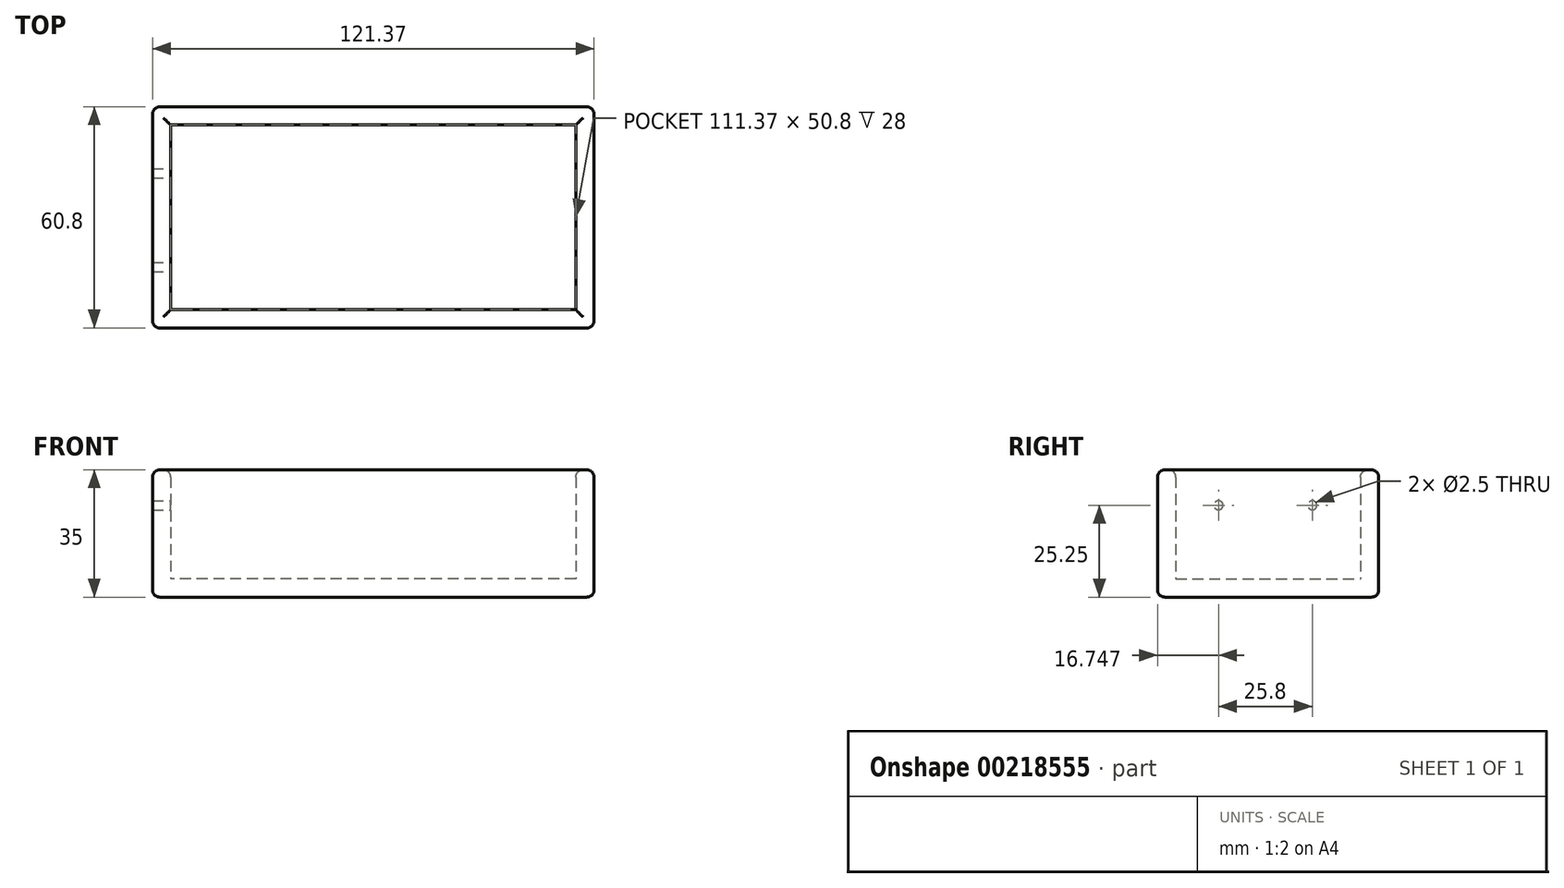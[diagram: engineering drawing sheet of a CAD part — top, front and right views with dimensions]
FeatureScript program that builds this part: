
annotation { "Feature Type Name" : "Feature", "Feature Type Description" : "" }
export const myFeature = defineFeature(function(context is Context, id is Id, definition is map)
    precondition{}
    {
        {
            var Q0;
            Q0=qCreatedBy(makeId("Top.planeOp"),FACE);
            var sketch = newSketch(context, id + "F0", { "sketchPlane" : qUnion([Q0])});
            skLineSegment(sketch, "E0.bottom", {"start": v(-56.15, 22.89) * mm, "end": v(55.22, 22.89) * mm});
            skLineSegment(sketch, "E0.top", {"start": v(-56.15, -27.91) * mm, "end": v(55.22, -27.91) * mm});
            skLineSegment(sketch, "E0.left", {"start": v(-56.15, 22.89) * mm, "end": v(-56.15, -27.91) * mm});
            skLineSegment(sketch, "E0.right", {"start": v(55.22, 22.89) * mm, "end": v(55.22, -27.91) * mm});
            skLineSegment(sketch, "E1.0", {"start": v(-61.15, 27.89) * mm, "end": v(60.22, 27.89) * mm});
            skLineSegment(sketch, "E1.1", {"start": v(-61.15, 27.89) * mm, "end": v(-61.15, -32.91) * mm});
            skLineSegment(sketch, "E1.2", {"start": v(-61.15, -32.91) * mm, "end": v(60.22, -32.91) * mm});
            skLineSegment(sketch, "E1.3", {"start": v(60.22, 27.89) * mm, "end": v(60.22, -32.91) * mm});
            skSolve(sketch);
        }
        {
            var Q0;
            Q0=makeQuery(id+"F0.imprint","IMPRINT",FACE,{"disambiguationData":[TD([[makeQuery(id+"F0.imprint","IMPRINT",EDGE,{"derivedFrom":sQuery(id+"F0.wireOp",EDGE,"E0.bottom")}),1.0]])]});
            var Q1;
            Q1=makeQuery(id+"F0.imprint","IMPRINT",FACE,{"disambiguationData":[TD([[makeQuery(id+"F0.imprint","IMPRINT",EDGE,{"derivedFrom":sQuery(id+"F0.wireOp",EDGE,"E0.bottom")}),-1.0]])]});
            extrude(context, id + "F1", {"entities" : qUnion([Q0, Q1]), "depth" : 5 * mm});
        }
        {
            var Q0;
            Q0=makeQuery(id+"F0.imprint","IMPRINT",FACE,{"disambiguationData":[TD([[makeQuery(id+"F0.imprint","IMPRINT",EDGE,{"derivedFrom":sQuery(id+"F0.wireOp",EDGE,"E0.bottom")}),1.0]])]});
            extrude(context, id + "F2", {"entities" : qUnion([Q0]), "operationType" : NewBodyOperationType.ADD, "depth" : 35 * mm});
        }
        {
            var Q0;
            Q0=qCreatedBy(makeId("Right.planeOp"),FACE);
            var sketch = newSketch(context, id + "F3", { "sketchPlane" : qUnion([Q0])});
            skCircle(sketch, "E2", {"center": v(-16.16, 25.25) * mm, "radius": 1.25 * mm});
            skCircle(sketch, "E3", {"center": v(9.64, 25.25) * mm, "radius": 1.25 * mm});
            skSolve(sketch);
        }
        {
            var Q0;
            Q0=makeQuery(id+"F3.imprint","IMPRINT",FACE,{"disambiguationData":[TD([[makeQuery(id+"F3.imprint","IMPRINT",EDGE,{"derivedFrom":sQuery(id+"F3.wireOp",EDGE,"E2")}),1.0]])]});
            var Q1;
            Q1=makeQuery(id+"F3.imprint","IMPRINT",FACE,{"disambiguationData":[TD([[makeQuery(id+"F3.imprint","IMPRINT",EDGE,{"derivedFrom":sQuery(id+"F3.wireOp",EDGE,"E3")}),1.0]])]});
            extrude(context, id + "F4", {"entities" : qUnion([Q0, Q1]), "operationType" : NewBodyOperationType.REMOVE, "oppositeDirection" : true, "depth" : 75 * mm});
        }
        {
            var Q0;
            {var subQ0=sQuery(id+"F0.wireOp",EDGE,"E1.2");Q0=makeQuery(id+"F2.boolean.opBoolean","MERGE",FACE,{"derivedFrom":[makeQuery(id+"F1.opExtrude","SWEPT_FACE",FACE,{"disambiguationData":[OSD([subQ0])]}),makeQuery(id+"F2.opExtrude","SWEPT_FACE",FACE,{"disambiguationData":[OSD([subQ0])]})]});}
            var Q1;
            {var subQ0=sQuery(id+"F0.wireOp",EDGE,"E1.0");Q1=makeQuery(id+"F2.boolean.opBoolean","MERGE",FACE,{"derivedFrom":[makeQuery(id+"F1.opExtrude","SWEPT_FACE",FACE,{"disambiguationData":[OSD([subQ0])]}),makeQuery(id+"F2.opExtrude","SWEPT_FACE",FACE,{"disambiguationData":[OSD([subQ0])]})]});}
            var Q2;
            {var subQ0=sQuery(id+"F0.wireOp",EDGE,"E1.3");Q2=makeQuery(id+"F2.boolean.opBoolean","MERGE",FACE,{"derivedFrom":[makeQuery(id+"F1.opExtrude","SWEPT_FACE",FACE,{"disambiguationData":[OSD([subQ0])]}),makeQuery(id+"F2.opExtrude","SWEPT_FACE",FACE,{"disambiguationData":[OSD([subQ0])]})]});}
            var Q3;
            Q3=makeQuery(id+"F2.opExtrude","CAP_EDGE",EDGE,{"disambiguationData":[OSD([sQuery(id+"F0.wireOp",EDGE,"E0.right")])],"isStart":false});
            var Q4;
            Q4=makeQuery(id+"F2.opExtrude","CAP_EDGE",EDGE,{"disambiguationData":[OSD([sQuery(id+"F0.wireOp",EDGE,"E0.bottom")])],"isStart":false});
            var Q5;
            Q5=makeQuery(id+"F2.opExtrude","CAP_EDGE",EDGE,{"disambiguationData":[OSD([sQuery(id+"F0.wireOp",EDGE,"E0.left")])],"isStart":false});
            var Q6;
            Q6=makeQuery(id+"F2.opExtrude","CAP_EDGE",EDGE,{"disambiguationData":[OSD([sQuery(id+"F0.wireOp",EDGE,"E0.top")])],"isStart":false});
            var Q7;
            Q7=makeQuery(id+"F2.opExtrude","CAP_EDGE",EDGE,{"disambiguationData":[OSD([sQuery(id+"F0.wireOp",EDGE,"E1.1")])],"isStart":false});
            var Q8;
            {var subQ0=sQuery(id+"F0.wireOp",EDGE,"E1.1");var subQ1=sQuery(id+"F0.wireOp",EDGE,"E1.0");Q8=makeQuery(id+"F2.boolean.opBoolean","MERGE",EDGE,{"derivedFrom":[makeQuery(id+"F1.opExtrude","SWEPT_EDGE",EDGE,{"disambiguationData":[OSD([subQ1,subQ0])]}),makeQuery(id+"F2.opExtrude","SWEPT_EDGE",EDGE,{"disambiguationData":[OSD([subQ1,subQ0])]})]});}
            var Q9;
            {var subQ0=sQuery(id+"F0.wireOp",EDGE,"E1.2");var subQ1=sQuery(id+"F0.wireOp",EDGE,"E1.1");Q9=makeQuery(id+"F2.boolean.opBoolean","MERGE",EDGE,{"derivedFrom":[makeQuery(id+"F1.opExtrude","SWEPT_EDGE",EDGE,{"disambiguationData":[OSD([subQ1,subQ0])]}),makeQuery(id+"F2.opExtrude","SWEPT_EDGE",EDGE,{"disambiguationData":[OSD([subQ1,subQ0])]})]});}
            var Q10;
            Q10=makeQuery(id+"F1.opExtrude","CAP_EDGE",EDGE,{"disambiguationData":[OSD([sQuery(id+"F0.wireOp",EDGE,"E1.1")])],"isStart":true});
            fillet(context, id + "F5", {"entities" : qUnion([Q0, Q1, Q2, Q3, Q4, Q5, Q6, Q7, Q8, Q9, Q10]), "radius" : 2 * mm, "tangentPropagation" : true, "allowEdgeOverflow" : false});
        }
    });
